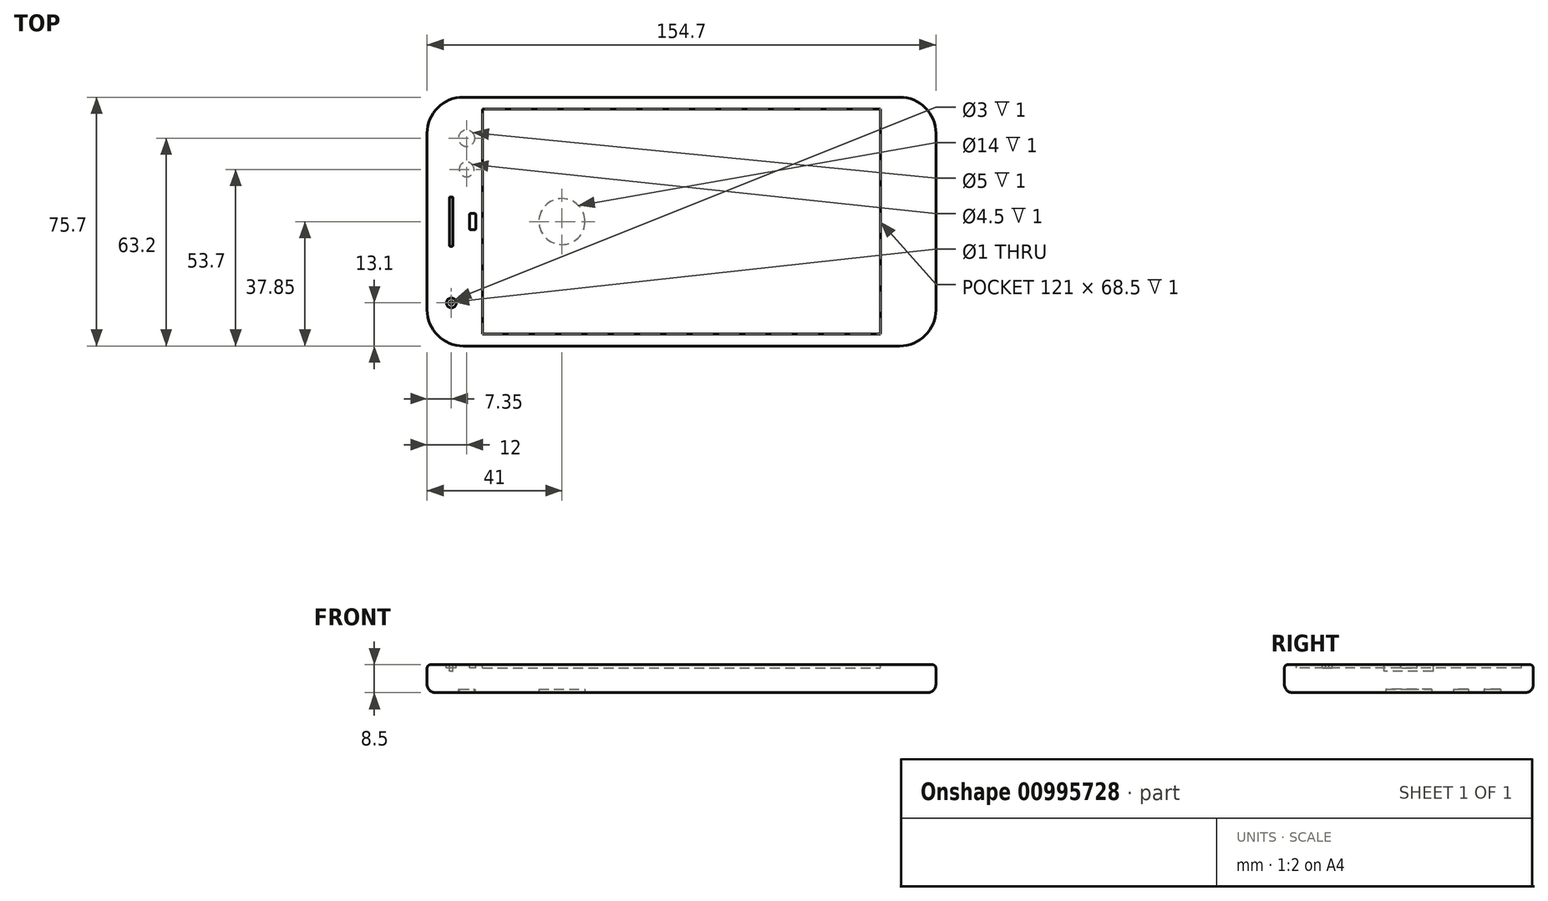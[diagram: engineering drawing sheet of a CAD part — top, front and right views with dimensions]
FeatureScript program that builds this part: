
annotation { "Feature Type Name" : "Feature", "Feature Type Description" : "" }
export const myFeature = defineFeature(function(context is Context, id is Id, definition is map)
    precondition{}
    {
        {
            var Q0;
            Q0=qCreatedBy(makeId("Top.planeOp"),FACE);
            var sketch = newSketch(context, id + "F0", { "sketchPlane" : qUnion([Q0])});
            skLineSegment(sketch, "E0.bottom", {"start": v(66.35, 37.85) * mm, "end": v(-66.35, 37.85) * mm});
            skLineSegment(sketch, "E0.top", {"start": v(66.35, -37.85) * mm, "end": v(-66.35, -37.85) * mm});
            skLineSegment(sketch, "E0.left", {"start": v(77.35, 26.85) * mm, "end": v(77.35, -26.85) * mm});
            skLineSegment(sketch, "E0.right", {"start": v(-77.35, 26.85) * mm, "end": v(-77.35, -26.85) * mm});
            skPoint(sketch, "E0.middle", {"position": v(0, 0) * mm});
            skPoint(sketch, "E1.visualSharp", {"position": v(-77.35, 37.85) * mm});
            skArc(sketch, "E1.filletArc", {"start": v(-66.35, 37.85) * mm, "mid": v(-74.13, 34.63) * mm, "end": v(-77.35, 26.85) * mm});
            skPoint(sketch, "E2.visualSharp", {"position": v(77.35, 37.85) * mm});
            skArc(sketch, "E2.filletArc", {"start": v(77.35, 26.85) * mm, "mid": v(74.13, 34.63) * mm, "end": v(66.35, 37.85) * mm});
            skPoint(sketch, "E3.visualSharp", {"position": v(-77.35, -37.85) * mm});
            skArc(sketch, "E3.filletArc", {"start": v(-77.35, -26.85) * mm, "mid": v(-74.13, -34.63) * mm, "end": v(-66.35, -37.85) * mm});
            skPoint(sketch, "E4.visualSharp", {"position": v(77.35, -37.85) * mm});
            skArc(sketch, "E4.filletArc", {"start": v(66.35, -37.85) * mm, "mid": v(74.13, -34.63) * mm, "end": v(77.35, -26.85) * mm});
            skSolve(sketch);
        }
        {
            var Q0;
            Q0=makeQuery(id+"F0.imprint","IMPRINT",FACE,{"disambiguationData":[TD([[makeQuery(id+"F0.imprint","IMPRINT",EDGE,{"derivedFrom":sQuery(id+"F0.wireOp",EDGE,"E0.bottom")}),1.0]])]});
            extrude(context, id + "F1", {"entities" : qUnion([Q0]), "depth" : 8.5 * mm, "offsetDistance" : 25 * mm});
        }
        {
            var Q0;
            Q0=makeQuery(id+"F1.opExtrude","CAP_FACE",FACE,{"disambiguationData":[OSD([sQuery(id+"F0.wireOp",EDGE,"E0.bottom"),sQuery(id+"F0.wireOp",EDGE,"E0.top"),sQuery(id+"F0.wireOp",EDGE,"E0.left"),sQuery(id+"F0.wireOp",EDGE,"E0.right"),sQuery(id+"F0.wireOp",EDGE,"E1.filletArc"),sQuery(id+"F0.wireOp",EDGE,"E2.filletArc"),sQuery(id+"F0.wireOp",EDGE,"E3.filletArc"),sQuery(id+"F0.wireOp",EDGE,"E4.filletArc")])],"isStart":false});
            var sketch = newSketch(context, id + "F2", { "sketchPlane" : qUnion([Q0])});
            skLineSegment(sketch, "E5.0", {"start": v(66.35, 37.85) * mm, "end": v(-66.35, 37.85) * mm});
            skLineSegment(sketch, "E6.0", {"start": v(-77.35, 26.85) * mm, "end": v(-77.35, -26.85) * mm});
            skLineSegment(sketch, "E7.bottom", {"start": v(-60.5, 34.25) * mm, "end": v(60.5, 34.25) * mm});
            skLineSegment(sketch, "E7.top", {"start": v(-60.5, -34.25) * mm, "end": v(60.5, -34.25) * mm});
            skLineSegment(sketch, "E7.left", {"start": v(-60.5, 34.25) * mm, "end": v(-60.5, -34.25) * mm});
            skLineSegment(sketch, "E7.right", {"start": v(60.5, 34.25) * mm, "end": v(60.5, -34.25) * mm});
            skCircle(sketch, "E8", {"center": v(-70, -24.75) * mm, "radius": 0.5 * mm});
            skCircle(sketch, "E9", {"center": v(-70, -24.75) * mm, "radius": 1.5 * mm});
            skLineSegment(sketch, "E10.bottom", {"start": v(-69.7, 7.5) * mm, "end": v(-70.3, 7.5) * mm});
            skLineSegment(sketch, "E10.top", {"start": v(-69.7, -7.5) * mm, "end": v(-70.3, -7.5) * mm});
            skLineSegment(sketch, "E10.left", {"start": v(-69.5, 7.3) * mm, "end": v(-69.5, -7.3) * mm});
            skLineSegment(sketch, "E10.right", {"start": v(-70.5, 7.3) * mm, "end": v(-70.5, -7.3) * mm});
            skLineSegment(sketch, "E11", {"start": v(-77.35, 0) * mm, "end": v(17.11, 0) * mm, "construction": true});
            skPoint(sketch, "E12.visualSharp", {"position": v(-70.5, 7.5) * mm});
            skArc(sketch, "E12.filletArc", {"start": v(-70.3, 7.5) * mm, "mid": v(-70.44, 7.44) * mm, "end": v(-70.5, 7.3) * mm});
            skPoint(sketch, "E13.visualSharp", {"position": v(-70.5, -7.5) * mm});
            skArc(sketch, "E13.filletArc", {"start": v(-70.5, -7.3) * mm, "mid": v(-70.44, -7.44) * mm, "end": v(-70.3, -7.5) * mm});
            skPoint(sketch, "E14.visualSharp", {"position": v(-69.5, 7.5) * mm});
            skArc(sketch, "E14.filletArc", {"start": v(-69.5, 7.3) * mm, "mid": v(-69.56, 7.44) * mm, "end": v(-69.7, 7.5) * mm});
            skPoint(sketch, "E15.visualSharp", {"position": v(-69.5, -7.5) * mm});
            skArc(sketch, "E15.filletArc", {"start": v(-69.7, -7.5) * mm, "mid": v(-69.56, -7.44) * mm, "end": v(-69.5, -7.3) * mm});
            skLineSegment(sketch, "E16.bottom", {"start": v(-63, -2.5) * mm, "end": v(-64, -2.5) * mm});
            skLineSegment(sketch, "E16.top", {"start": v(-63, 2.5) * mm, "end": v(-64, 2.5) * mm});
            skLineSegment(sketch, "E16.left", {"start": v(-62.5, -2) * mm, "end": v(-62.5, 2) * mm});
            skLineSegment(sketch, "E16.right", {"start": v(-64.5, -2) * mm, "end": v(-64.5, 2) * mm});
            skPoint(sketch, "E17.visualSharp", {"position": v(-64.5, 2.5) * mm});
            skArc(sketch, "E17.filletArc", {"start": v(-64, 2.5) * mm, "mid": v(-64.35, 2.35) * mm, "end": v(-64.5, 2) * mm});
            skPoint(sketch, "E18.visualSharp", {"position": v(-62.5, 2.5) * mm});
            skArc(sketch, "E18.filletArc", {"start": v(-62.5, 2) * mm, "mid": v(-62.65, 2.35) * mm, "end": v(-63, 2.5) * mm});
            skPoint(sketch, "E19.visualSharp", {"position": v(-62.5, -2.5) * mm});
            skArc(sketch, "E19.filletArc", {"start": v(-63, -2.5) * mm, "mid": v(-62.65, -2.35) * mm, "end": v(-62.5, -2) * mm});
            skPoint(sketch, "E20.visualSharp", {"position": v(-64.5, -2.5) * mm});
            skArc(sketch, "E20.filletArc", {"start": v(-64.5, -2) * mm, "mid": v(-64.35, -2.35) * mm, "end": v(-64, -2.5) * mm});
            skSolve(sketch);
        }
        {
            var Q0;
            Q0=makeQuery(id+"F2.imprint","IMPRINT",FACE,{"disambiguationData":[TD([[makeQuery(id+"F2.imprint","IMPRINT",EDGE,{"derivedFrom":sQuery(id+"F2.wireOp",EDGE,"E7.bottom")}),-1.0]])]});
            extrude(context, id + "F3", {"entities" : qUnion([Q0]), "operationType" : NewBodyOperationType.REMOVE, "oppositeDirection" : true, "depth" : 1 * mm, "offsetDistance" : 25 * mm});
        }
        {
            var Q0;
            Q0=makeQuery(id+"F2.imprint","IMPRINT",FACE,{"disambiguationData":[TD([[makeQuery(id+"F2.imprint","IMPRINT",EDGE,{"derivedFrom":sQuery(id+"F2.wireOp",EDGE,"E7.bottom")}),-1.0]])]});
            extrude(context, id + "F4", {"entities" : qUnion([Q0]), "oppositeDirection" : true, "depth" : 1 * mm, "offsetDistance" : 25 * mm});
        }
        {
            var Q0;
            Q0=makeQuery(id+"F2.imprint","IMPRINT",FACE,{"disambiguationData":[TD([[makeQuery(id+"F2.imprint","IMPRINT",EDGE,{"derivedFrom":sQuery(id+"F2.wireOp",EDGE,"E8")}),-1.0]])]});
            extrude(context, id + "F5", {"entities" : qUnion([Q0]), "operationType" : NewBodyOperationType.REMOVE, "oppositeDirection" : true, "depth" : 1 * mm, "offsetDistance" : 25 * mm});
        }
        {
            var Q0;
            Q0=makeQuery(id+"F2.imprint","IMPRINT",FACE,{"disambiguationData":[TD([[makeQuery(id+"F2.imprint","IMPRINT",EDGE,{"derivedFrom":sQuery(id+"F2.wireOp",EDGE,"E8")}),-1.0]])]});
            extrude(context, id + "F6", {"entities" : qUnion([Q0]), "oppositeDirection" : true, "depth" : 1 * mm, "offsetDistance" : 25 * mm});
        }
        {
            var Q0;
            Q0=makeQuery(id+"F1.opExtrude","CAP_FACE",FACE,{"disambiguationData":[OSD([sQuery(id+"F0.wireOp",EDGE,"E0.bottom"),sQuery(id+"F0.wireOp",EDGE,"E0.top"),sQuery(id+"F0.wireOp",EDGE,"E0.left"),sQuery(id+"F0.wireOp",EDGE,"E0.right"),sQuery(id+"F0.wireOp",EDGE,"E1.filletArc"),sQuery(id+"F0.wireOp",EDGE,"E2.filletArc"),sQuery(id+"F0.wireOp",EDGE,"E3.filletArc"),sQuery(id+"F0.wireOp",EDGE,"E4.filletArc")])],"isStart":true});
            var sketch = newSketch(context, id + "F7", { "sketchPlane" : qUnion([Q0])});
            skCircle(sketch, "E21", {"center": v(-36.35, 0) * mm, "radius": 7 * mm});
            skLineSegment(sketch, "E22.0", {"start": v(66.35, -37.85) * mm, "end": v(-66.35, -37.85) * mm, "construction": true});
            skLineSegment(sketch, "E23.0", {"start": v(66.35, 37.85) * mm, "end": v(-66.35, 37.85) * mm, "construction": true});
            skLineSegment(sketch, "E24.0", {"start": v(-77.35, -26.85) * mm, "end": v(-77.35, 26.85) * mm, "construction": true});
            skCircle(sketch, "E25", {"center": v(-65.35, -25.35) * mm, "radius": 2.5 * mm});
            skLineSegment(sketch, "E26", {"start": v(-77.35, 0) * mm, "end": v(77.35, 0) * mm, "construction": true});
            skCircle(sketch, "E27", {"center": v(-65.35, -15.85) * mm, "radius": 2.25 * mm});
            skSolve(sketch);
        }
        {
            var Q0;
            Q0=makeQuery(id+"F7.imprint","IMPRINT",FACE,{"disambiguationData":[TD([[makeQuery(id+"F7.imprint","IMPRINT",EDGE,{"derivedFrom":sQuery(id+"F7.wireOp",EDGE,"E21")}),1.0]])]});
            extrude(context, id + "F8", {"entities" : qUnion([Q0]), "operationType" : NewBodyOperationType.REMOVE, "oppositeDirection" : true, "depth" : 1 * mm, "offsetDistance" : 25 * mm});
        }
        {
            var Q0;
            Q0=makeQuery(id+"F7.imprint","IMPRINT",FACE,{"disambiguationData":[TD([[makeQuery(id+"F7.imprint","IMPRINT",EDGE,{"derivedFrom":sQuery(id+"F7.wireOp",EDGE,"E21")}),1.0]])]});
            extrude(context, id + "F9", {"entities" : qUnion([Q0]), "oppositeDirection" : true, "depth" : 1 * mm, "offsetDistance" : 25 * mm});
        }
        {
            var Q0;
            Q0=makeQuery(id+"F1.opExtrude","CAP_EDGE",EDGE,{"disambiguationData":[OSD([sQuery(id+"F0.wireOp",EDGE,"E0.right")])],"isStart":false});
            fillet(context, id + "F10", {"entities" : qUnion([Q0]), "radius" : 1 * mm, "tangentPropagation" : true, "allowEdgeOverflow" : false});
        }
        {
            var Q0;
            Q0=makeQuery(id+"F1.opExtrude","CAP_EDGE",EDGE,{"disambiguationData":[OSD([sQuery(id+"F0.wireOp",EDGE,"E0.top")])],"isStart":true});
            fillet(context, id + "F11", {"entities" : qUnion([Q0]), "radius" : 2.5 * mm, "tangentPropagation" : true, "allowEdgeOverflow" : false});
        }
        {
            var Q0;
            Q0=makeQuery(id+"F2.imprint","IMPRINT",FACE,{"disambiguationData":[TD([[makeQuery(id+"F2.imprint","IMPRINT",EDGE,{"derivedFrom":sQuery(id+"F2.wireOp",EDGE,"E10.bottom")}),1.0]])]});
            extrude(context, id + "F12", {"entities" : qUnion([Q0]), "operationType" : NewBodyOperationType.REMOVE, "oppositeDirection" : true, "depth" : 2 * mm, "offsetDistance" : 25 * mm});
        }
        {
            var Q0;
            Q0=makeQuery(id+"F2.imprint","IMPRINT",FACE,{"disambiguationData":[TD([[makeQuery(id+"F2.imprint","IMPRINT",EDGE,{"derivedFrom":sQuery(id+"F2.wireOp",EDGE,"E16.bottom")}),-1.0]])]});
            extrude(context, id + "F13", {"entities" : qUnion([Q0]), "operationType" : NewBodyOperationType.REMOVE, "oppositeDirection" : true, "depth" : 1 * mm, "offsetDistance" : 25 * mm});
        }
        {
            var Q0;
            Q0=makeQuery(id+"F13.boolean.opBoolean","COPY",FACE,{"derivedFrom":makeQuery(id+"F13.opExtrude","CAP_FACE",FACE,{"disambiguationData":[OSD([sQuery(id+"F2.wireOp",EDGE,"E16.bottom"),sQuery(id+"F2.wireOp",EDGE,"E16.top"),sQuery(id+"F2.wireOp",EDGE,"E16.left"),sQuery(id+"F2.wireOp",EDGE,"E16.right"),sQuery(id+"F2.wireOp",EDGE,"E17.filletArc"),sQuery(id+"F2.wireOp",EDGE,"E18.filletArc"),sQuery(id+"F2.wireOp",EDGE,"E19.filletArc"),sQuery(id+"F2.wireOp",EDGE,"E20.filletArc")])],"isStart":false})});
            extrude(context, id + "F14", {"entities" : qUnion([Q0]), "depth" : 1 * mm, "offsetDistance" : 25 * mm});
        }
        {
            var Q0;
            Q0=makeQuery(id+"F7.imprint","IMPRINT",FACE,{"disambiguationData":[TD([[makeQuery(id+"F7.imprint","IMPRINT",EDGE,{"derivedFrom":sQuery(id+"F7.wireOp",EDGE,"E25")}),1.0]])]});
            extrude(context, id + "F15", {"entities" : qUnion([Q0]), "operationType" : NewBodyOperationType.REMOVE, "oppositeDirection" : true, "depth" : 1 * mm, "offsetDistance" : 25 * mm});
        }
        {
            var Q0;
            Q0=makeQuery(id+"F7.imprint","IMPRINT",FACE,{"disambiguationData":[TD([[makeQuery(id+"F7.imprint","IMPRINT",EDGE,{"derivedFrom":sQuery(id+"F7.wireOp",EDGE,"E25")}),1.0]])]});
            extrude(context, id + "F16", {"entities" : qUnion([Q0]), "oppositeDirection" : true, "depth" : 1 * mm, "offsetDistance" : 25 * mm});
        }
        {
            var Q0;
            Q0=makeQuery(id+"F7.imprint","IMPRINT",FACE,{"disambiguationData":[TD([[makeQuery(id+"F7.imprint","IMPRINT",EDGE,{"derivedFrom":sQuery(id+"F7.wireOp",EDGE,"E27")}),1.0]])]});
            extrude(context, id + "F17", {"entities" : qUnion([Q0]), "operationType" : NewBodyOperationType.REMOVE, "oppositeDirection" : true, "depth" : 1 * mm, "offsetDistance" : 25 * mm});
        }
        {
            var Q0;
            Q0=makeQuery(id+"F7.imprint","IMPRINT",FACE,{"disambiguationData":[TD([[makeQuery(id+"F7.imprint","IMPRINT",EDGE,{"derivedFrom":sQuery(id+"F7.wireOp",EDGE,"E27")}),1.0]])]});
            extrude(context, id + "F18", {"entities" : qUnion([Q0]), "oppositeDirection" : true, "depth" : 1 * mm, "offsetDistance" : 25 * mm});
        }
    });
